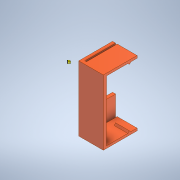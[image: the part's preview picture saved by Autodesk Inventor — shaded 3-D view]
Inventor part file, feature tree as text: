
AUTODESK INVENTOR PART (.ipt)
format: ipt  version: 2021.2 (Build 252289000, 289)  size: 586,752 bytes
history: native  units: in
note: dims shown in document units (in); Inventor stores cm internally (conversion verified against a paired STEP export)
features: extrude x7, sketch x7, mirror x1
ambient origin geometry x8: Origin, YZ Plane, XZ Plane, XY Plane, X Axis, Y Axis, Z Axis, Center Point
bodies: Solid1 (feature_tree)
feature tree (15):
  extrude  "Extrusion1"  Depth=0.8in
  extrude  "Extrusion7"  TaperAngle=0.0deg  [1 undecoded]
  extrude  "Extrusion8"  Depth=0.075in
  extrude  "Extrusion9"  Depth=0.6125in
  extrude  "Extrusion10"  Depth=0.1in
  extrude  "Extrusion11"  Depth=0.24in TaperAngle=0.0deg
  extrude  "Extrusion12"  TaperAngle=135.0deg  [1 undecoded]
  mirror  "Mirror1"
  sketch  "Sketch1"  dims[d0=2.125in d1=0.8in]
  sketch  "Sketch8"  dims[d2=0.1in d3=0.0in]
  sketch  "Sketch10"  dims[d32=0.075in d33=0.075in]
  sketch  "Sketch11"  dims[d34=0.1in d35=0.6125in]
  sketch  "Sketch12"  dims[d36=0.6125in d37=0.1in]
  sketch  "Sketch16"  dims[d38=1.0in d39=0.0in d40=0.24in d41=0.0in]
  sketch  "Sketch17"  dims[d42=90.0deg d43=135.0deg d44=0.05in d45=0.25in d46=0.24in d47=0.0in d48=0.05in d49=0.0in d50=0.0in d51=0.37in d52=0.05in d53=0.0in d54=0.75in d55=0.25in d56=0.0625in d57=0.0in]
note: 2 required parameter values undecoded (feature->parameter linkage not recoverable at this tier; creation-order binding heuristic only, values carry confidence <= 0.55)
